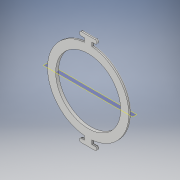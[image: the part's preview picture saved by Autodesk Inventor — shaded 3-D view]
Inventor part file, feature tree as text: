
AUTODESK INVENTOR PART (.ipt)
format: ipt  version: 2018 (Build 220112000, 112)  size: 2,299,904 bytes
history: native  units: mm
features: extrude x2, sketch x2, mirror x1, fillet x1, plane x1
ambient origin geometry x8: Origin, YZ Plane, XZ Plane, XY Plane, X Axis, Y Axis, Z Axis, Center Point
bodies: Volumenkörper1 (feature_tree)
feature tree (7):
  extrude  "Extrusion1"  Depth=88.0mm
  mirror  "Spiegeln1"
  extrude  "Extrusion2"  Depth=2.0mm
  fillet  "Rundung2"  Radius=2.5mm
  sketch  "Skizze1"  dims[d0=110.0mm d1=88.0mm]
  plane  "Arbeitsebene1"
  sketch  "Skizze2"  dims[d2=10.0mm d3=2.5mm d4=2.5mm d5=5.0mm d6=5.0mm d7=24.0mm d8=60.0mm d9=4.5mm d10=4.0mm d11=0.0mm d13=1.0mm d14=0.0mm d15=2.0mm]
